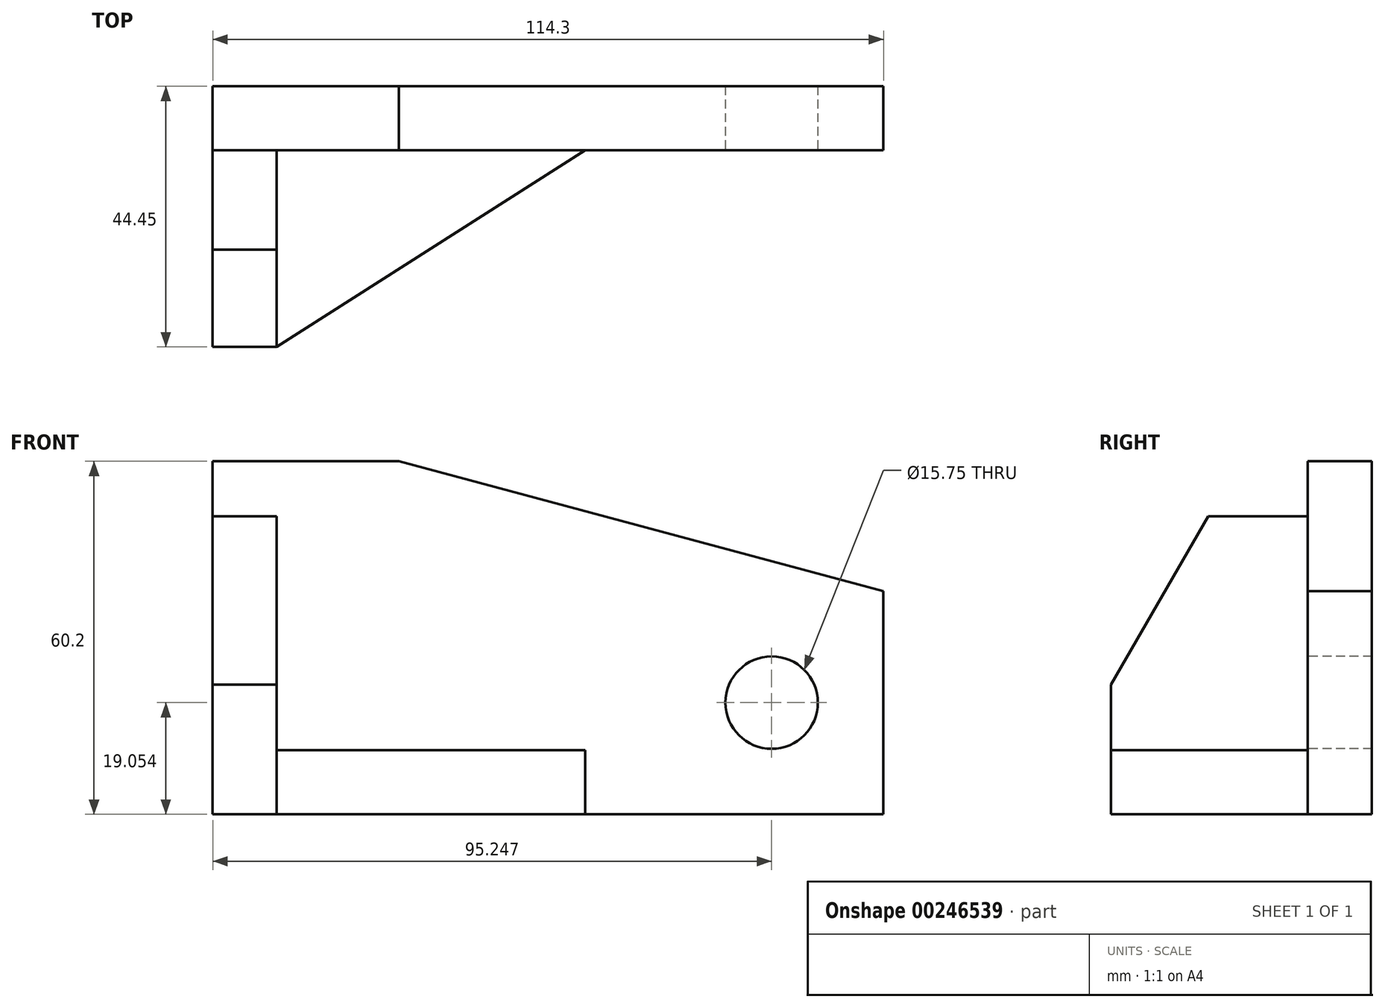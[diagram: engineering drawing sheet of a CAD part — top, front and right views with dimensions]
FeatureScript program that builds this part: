
annotation { "Feature Type Name" : "Feature", "Feature Type Description" : "" }
export const myFeature = defineFeature(function(context is Context, id is Id, definition is map)
    precondition{}
    {
        {
            var Q0;
            Q0=qCreatedBy(makeId("Front.planeOp"),FACE);
            var sketch = newSketch(context, id + "F0", { "sketchPlane" : qUnion([Q0])});
            skLineSegment(sketch, "E0.bottom", {"start": v(-60, 35.01) * mm, "end": v(54.3, 35.01) * mm});
            skLineSegment(sketch, "E0.top", {"start": v(-60, -25.19) * mm, "end": v(54.3, -25.19) * mm});
            skLineSegment(sketch, "E0.left", {"start": v(-60, 35.01) * mm, "end": v(-60, -25.19) * mm});
            skLineSegment(sketch, "E0.right", {"start": v(54.3, 35.01) * mm, "end": v(54.3, -25.19) * mm});
            skLineSegment(sketch, "E1", {"start": v(-60, 35.01) * mm, "end": v(-28.25, 35.01) * mm});
            skLineSegment(sketch, "E2", {"start": v(-28.25, 35.01) * mm, "end": v(54.3, 12.9) * mm});
            skSolve(sketch);
        }
        {
            var Q0;
            {var subQ1=sQuery(id+"F0.wireOp",EDGE,"E0.top");Q0=makeQuery(id+"F0.imprint","IMPRINT",FACE,{"disambiguationData":[TD([[makeQuery(id+"F0.imprint","IMPRINT",EDGE,{"derivedFrom":subQ1}),1.0]])]});}
            extrude(context, id + "F1", {"entities" : qUnion([Q0]), "depth" : 10.92 * mm});
        }
        {
            var Q0;
            Q0=makeQuery(id+"F1.opExtrude","CAP_FACE",FACE,{"disambiguationData":[OSD([sQuery(id+"F0.wireOp",EDGE,"E0.top"),sQuery(id+"F0.wireOp",EDGE,"E0.left"),sQuery(id+"F0.wireOp",EDGE,"E0.right"),sQuery(id+"F0.wireOp",EDGE,"E1"),sQuery(id+"F0.wireOp",EDGE,"E2")])],"isStart":false});
            var sketch = newSketch(context, id + "F2", { "sketchPlane" : qUnion([Q0])});
            skLineSegment(sketch, "E3.bottom", {"start": v(-49.08, -14.26) * mm, "end": v(3.5, -14.26) * mm});
            skLineSegment(sketch, "E3.top", {"start": v(-49.08, -25.19) * mm, "end": v(3.5, -25.19) * mm});
            skLineSegment(sketch, "E3.left", {"start": v(-49.08, -14.26) * mm, "end": v(-49.08, -25.19) * mm});
            skLineSegment(sketch, "E3.right", {"start": v(3.5, -14.26) * mm, "end": v(3.5, -25.19) * mm});
            skSolve(sketch);
        }
        {
            var Q0;
            Q0=makeQuery(id+"F2.imprint","IMPRINT",FACE,{"disambiguationData":[TD([[makeQuery(id+"F2.imprint","IMPRINT",EDGE,{"derivedFrom":sQuery(id+"F2.wireOp",EDGE,"E3.bottom")}),-1.0]])]});
            extrude(context, id + "F3", {"entities" : qUnion([Q0]), "operationType" : NewBodyOperationType.ADD, "depth" : 33.53 * mm});
        }
        {
            var Q0;
            Q0=makeQuery(id+"F1.opExtrude","CAP_FACE",FACE,{"disambiguationData":[OSD([sQuery(id+"F0.wireOp",EDGE,"E0.top"),sQuery(id+"F0.wireOp",EDGE,"E0.left"),sQuery(id+"F0.wireOp",EDGE,"E0.right"),sQuery(id+"F0.wireOp",EDGE,"E1"),sQuery(id+"F0.wireOp",EDGE,"E2")])],"isStart":false});
            var sketch = newSketch(context, id + "F4", { "sketchPlane" : qUnion([Q0])});
            skLineSegment(sketch, "E4.bottom", {"start": v(-60, 25.61) * mm, "end": v(-49.08, 25.61) * mm});
            skLineSegment(sketch, "E4.top", {"start": v(-60, -25.19) * mm, "end": v(-49.08, -25.19) * mm});
            skLineSegment(sketch, "E4.left", {"start": v(-60, 25.61) * mm, "end": v(-60, -25.19) * mm});
            skLineSegment(sketch, "E4.right", {"start": v(-49.08, 25.61) * mm, "end": v(-49.08, -25.19) * mm});
            skSolve(sketch);
        }
        {
            var Q0;
            {var subQ2=sQuery(id+"F4.wireOp",EDGE,"E4.bottom");Q0=makeQuery(id+"F4.imprint","IMPRINT",FACE,{"disambiguationData":[TD([[makeQuery(id+"F4.imprint","IMPRINT",EDGE,{"derivedFrom":subQ2}),-1.0]])]});}
            extrude(context, id + "F5", {"entities" : qUnion([Q0]), "operationType" : NewBodyOperationType.ADD, "depth" : 33.53 * mm});
        }
        {
            var Q0;
            Q0=makeQuery(id+"F5.opExtrude","SWEPT_FACE",FACE,{"disambiguationData":[OSD([sQuery(id+"F4.wireOp",EDGE,"E4.right")])]});
            var sketch = newSketch(context, id + "F6", { "sketchPlane" : qUnion([Q0])});
            skLineSegment(sketch, "E5", {"start": v(-44.45, -14.26) * mm, "end": v(-44.45, -3.09) * mm});
            skLineSegment(sketch, "E6", {"start": v(-44.45, -3.09) * mm, "end": v(-27.88, 25.61) * mm});
            skLineSegment(sketch, "E7", {"start": v(-27.88, 25.61) * mm, "end": v(-10.92, 25.61) * mm});
            skLineSegment(sketch, "E8", {"start": v(-10.92, 25.61) * mm, "end": v(-10.92, -14.26) * mm});
            skLineSegment(sketch, "E9", {"start": v(-10.92, -14.26) * mm, "end": v(-44.45, -14.26) * mm});
            skSolve(sketch);
        }
        {
            var Q0;
            {var subQ0=sQuery(id+"F6.wireOp",EDGE,"E6");Q0=makeQuery(id+"F6.imprint","IMPRINT",FACE,{"disambiguationData":[TD([[makeQuery(id+"F6.imprint","IMPRINT",EDGE,{"derivedFrom":subQ0}),1.0]])]});}
            extrude(context, id + "F7", {"entities" : qUnion([Q0]), "operationType" : NewBodyOperationType.REMOVE, "oppositeDirection" : true, "depth" : 25.4 * mm});
        }
        {
            var Q0;
            Q0=makeQuery(id+"F3.opExtrude","SWEPT_FACE",FACE,{"disambiguationData":[OSD([sQuery(id+"F2.wireOp",EDGE,"E3.bottom")])]});
            var sketch = newSketch(context, id + "F8", { "sketchPlane" : qUnion([Q0])});
            skLineSegment(sketch, "E10", {"start": v(-49.08, -44.45) * mm, "end": v(3.5, -10.92) * mm});
            skLineSegment(sketch, "E11", {"start": v(3.5, -10.92) * mm, "end": v(-49.08, -10.92) * mm});
            skLineSegment(sketch, "E12", {"start": v(-49.08, -10.92) * mm, "end": v(-49.08, -44.45) * mm});
            skSolve(sketch);
        }
        {
            var Q0;
            Q0=makeQuery(id+"F8.imprint","IMPRINT",FACE,{"disambiguationData":[TD([[makeQuery(id+"F8.imprint","IMPRINT",EDGE,{"derivedFrom":sQuery(id+"F8.wireOp",EDGE,"E10")}),-1.0]])]});
            extrude(context, id + "F9", {"entities" : qUnion([Q0]), "operationType" : NewBodyOperationType.REMOVE, "oppositeDirection" : true, "depth" : 25.4 * mm});
        }
        {
            var Q0;
            Q0=makeQuery(id+"F1.opExtrude","CAP_FACE",FACE,{"disambiguationData":[OSD([sQuery(id+"F0.wireOp",EDGE,"E0.top"),sQuery(id+"F0.wireOp",EDGE,"E0.left"),sQuery(id+"F0.wireOp",EDGE,"E0.right"),sQuery(id+"F0.wireOp",EDGE,"E1"),sQuery(id+"F0.wireOp",EDGE,"E2")])],"isStart":false});
            var sketch = newSketch(context, id + "F10", { "sketchPlane" : qUnion([Q0])});
            skCircle(sketch, "E13", {"center": v(35.25, -6.14) * mm, "radius": 7.87 * mm});
            skSolve(sketch);
        }
        {
            var Q0;
            Q0=sQuery(id+"F10.wireOp",VERTEX,"E13.center");
            var Q1;
            Q1=makeQuery(id+"F1.opExtrude","SWEPT_BODY",BODY,{"disambiguationData":[OSD([sQuery(id+"F0.wireOp",EDGE,"E0.top"),sQuery(id+"F0.wireOp",EDGE,"E0.left"),sQuery(id+"F0.wireOp",EDGE,"E0.right"),sQuery(id+"F0.wireOp",EDGE,"E1"),sQuery(id+"F0.wireOp",EDGE,"E2")])]});
            hole(context, id + "F11", {"style" : HoleStyle.SIMPLE, "endStyle" : HoleEndStyle.THROUGH, "holeDiameter" : 15.75 * mm, "tappedDepth" : 12.7 * mm, "tapClearance" : 3, "locations" : qUnion([Q0]), "scope" : qUnion([Q1])});
        }
    });
